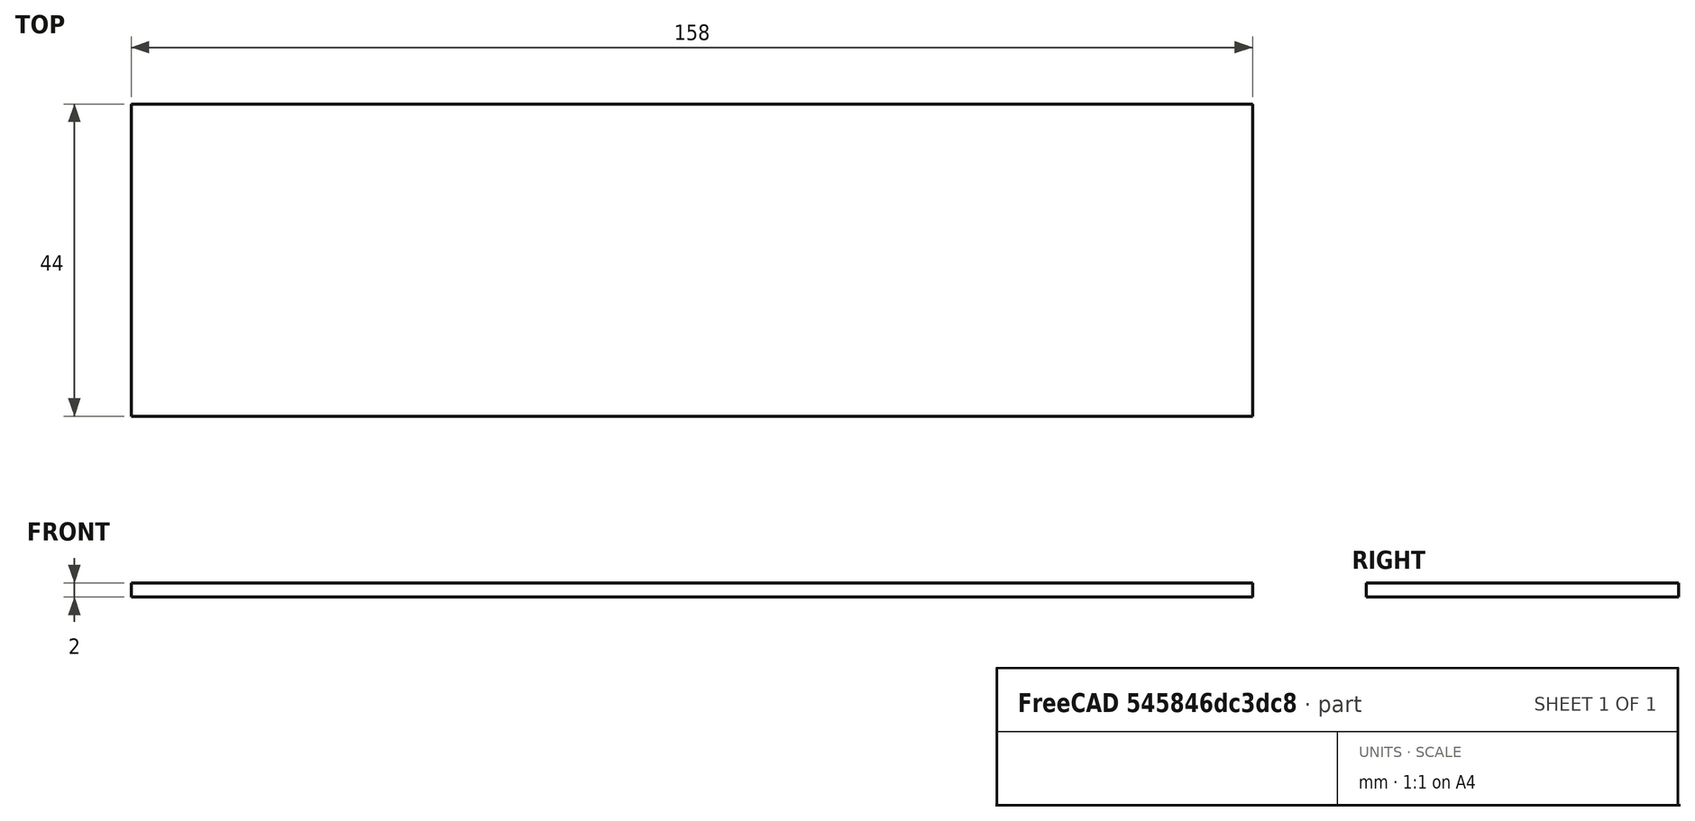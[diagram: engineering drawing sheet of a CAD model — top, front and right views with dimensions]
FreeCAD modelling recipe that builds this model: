
FCSTD DOCUMENT  (FreeCAD 0.21R33771 (Git))
Label: design attempt 1.1
License: All rights reserved
LicenseURL: https://en.wikipedia.org/wiki/All_rights_reserved
objects: Sketcher::SketchObject×2, PartDesign::Pad×1, PartDesign::Body×1
note: 5 computed .brp shape members not serialized (recipe doc carries the construction recipe); baked Part::Feature solids carry a one-line shape summary decoded from their .brp

FEATURE [Sketcher::SketchObject] Sketch
  FullyConstrained = false
  MapMode = 5
  Support = -> [XY_Plane]
  sketch-geometry (116):
    g0: LineSegment StartX=0 StartY=44 StartZ=0 EndX=20 EndY=44 EndZ=0
    g1: LineSegment StartX=158 StartY=0 StartZ=0 EndX=138 EndY=0 EndZ=0
    g2: LineSegment StartX=158 StartY=44 StartZ=0 EndX=138 EndY=44 EndZ=0
    g3: LineSegment StartX=1 StartY=2 StartZ=0 EndX=1 EndY=6.3 EndZ=0
    g4: LineSegment StartX=1 StartY=6.3 StartZ=0 EndX=2 EndY=6.3 EndZ=0
    g5: LineSegment StartX=2 StartY=6.3 StartZ=0 EndX=2 EndY=2 EndZ=0
    g6: LineSegment StartX=20 StartY=21 StartZ=0 EndX=20 EndY=23 EndZ=0
    g7: LineSegment StartX=1 StartY=21 StartZ=0 EndX=1 EndY=16.7 EndZ=0
    g8: LineSegment StartX=1 StartY=16.7 StartZ=0 EndX=2 EndY=16.7 EndZ=0
    g9: LineSegment StartX=2 StartY=16.7 StartZ=0 EndX=2 EndY=21 EndZ=0
    g10: LineSegment StartX=76.5 StartY=2 StartZ=0 EndX=76.5 EndY=6.3 EndZ=0
    g11: LineSegment StartX=76.5 StartY=6.3 StartZ=0 EndX=75.5 EndY=6.3 EndZ=0
    g12: LineSegment StartX=75.5 StartY=6.3 StartZ=0 EndX=75.5 EndY=2 EndZ=0
    g13: LineSegment StartX=77.5 StartY=0 StartZ=0 EndX=79.5 EndY=0 EndZ=0
    g14: LineSegment StartX=79.4989 StartY=44 StartZ=0 EndX=77.4989 EndY=44 EndZ=0
    g15: LineSegment StartX=77.5 StartY=0 StartZ=0 EndX=57.5 EndY=0 EndZ=0
    g16: LineSegment StartX=76.5 StartY=21 StartZ=0 EndX=76.5 EndY=16.7 EndZ=0
    g17: LineSegment StartX=76.5 StartY=16.7 StartZ=0 EndX=75.5 EndY=16.7 EndZ=0
    g18: LineSegment StartX=75.5 StartY=16.7 StartZ=0 EndX=75.5 EndY=21 EndZ=0
    g19: LineSegment StartX=57.5 StartY=21 StartZ=0 EndX=57.5 EndY=23 EndZ=0
    g20: LineSegment StartX=2 StartY=23 StartZ=0 EndX=2 EndY=27.3 EndZ=0
    g21: LineSegment StartX=2 StartY=27.3 StartZ=0 EndX=1 EndY=27.3 EndZ=0
    g22: LineSegment StartX=1 StartY=27.3 StartZ=0 EndX=1 EndY=23 EndZ=0
    g23: LineSegment StartX=2 StartY=42 StartZ=0 EndX=2 EndY=37.7 EndZ=0
    g24: LineSegment StartX=2 StartY=37.7 StartZ=0 EndX=1 EndY=37.7 EndZ=0
    g25: LineSegment StartX=1 StartY=37.7 StartZ=0 EndX=1 EndY=42 EndZ=0
    g26: LineSegment StartX=57.5 StartY=44 StartZ=0 EndX=77.5 EndY=44 EndZ=0
    g27: LineSegment StartX=76.5 StartY=23 StartZ=0 EndX=76.5 EndY=27.3 EndZ=0
    g28: LineSegment StartX=76.5 StartY=27.3 StartZ=0 EndX=75.5 EndY=27.3 EndZ=0
    g29: LineSegment StartX=75.5 StartY=27.3 StartZ=0 EndX=75.5 EndY=23 EndZ=0
    g30: LineSegment StartX=75.5 StartY=42 StartZ=0 EndX=75.5 EndY=37.7 EndZ=0
    g31: LineSegment StartX=75.5 StartY=37.7 StartZ=0 EndX=76.5 EndY=37.7 EndZ=0
    g32: LineSegment StartX=76.5 StartY=37.7 StartZ=0 EndX=76.5 EndY=42 EndZ=0
    g33: LineSegment StartX=79.5 StartY=0 StartZ=0 EndX=99.5 EndY=0 EndZ=0
    g34: LineSegment StartX=79.5 StartY=44 StartZ=0 EndX=99.5 EndY=44 EndZ=0
    g35: LineSegment StartX=99.5 StartY=23 StartZ=0 EndX=99.5 EndY=21 EndZ=0
    g36: LineSegment StartX=138 StartY=21 StartZ=0 EndX=138 EndY=23 EndZ=0
    g37: LineSegment StartX=81.5 StartY=2 StartZ=0 EndX=81.5 EndY=6.3 EndZ=0
    g38: LineSegment StartX=81.5 StartY=6.3 StartZ=0 EndX=80.5 EndY=6.3 EndZ=0
    g39: LineSegment StartX=80.5 StartY=6.3 StartZ=0 EndX=80.5 EndY=2 EndZ=0
    g40: LineSegment StartX=81.5 StartY=21 StartZ=0 EndX=81.5 EndY=16.7 EndZ=0
    g41: LineSegment StartX=81.5 StartY=16.7 StartZ=0 EndX=80.5 EndY=16.7 EndZ=0
    g42: LineSegment StartX=80.5 StartY=16.7 StartZ=0 EndX=80.5 EndY=21 EndZ=0
    g43: LineSegment StartX=80.5 StartY=23 StartZ=0 EndX=80.5 EndY=27.3 EndZ=0
    g44: LineSegment StartX=80.5 StartY=27.3 StartZ=0 EndX=81.5 EndY=27.3 EndZ=0
    g45: LineSegment StartX=81.5 StartY=27.3 StartZ=0 EndX=81.5 EndY=23 EndZ=0
    g46: LineSegment StartX=156 StartY=2 StartZ=0 EndX=156 EndY=6.3 EndZ=0
    g47: LineSegment StartX=156 StartY=6.3 StartZ=0 EndX=157 EndY=6.3 EndZ=0
    g48: LineSegment StartX=157 StartY=6.3 StartZ=0 EndX=157 EndY=2 EndZ=0
    g49: LineSegment StartX=156 StartY=21 StartZ=0 EndX=156 EndY=16.7 EndZ=0
    g50: LineSegment StartX=156 StartY=16.7 StartZ=0 EndX=157 EndY=16.7 EndZ=0
    g51: LineSegment StartX=157 StartY=16.7 StartZ=0 EndX=157 EndY=21 EndZ=0
    g52: LineSegment StartX=156 StartY=23 StartZ=0 EndX=156 EndY=27.3 EndZ=0
    g53: LineSegment StartX=156 StartY=27.3 StartZ=0 EndX=157 EndY=27.3 EndZ=0
    g54: LineSegment StartX=157 StartY=27.3 StartZ=0 EndX=157 EndY=23 EndZ=0
    g55: LineSegment StartX=156 StartY=42 StartZ=0 EndX=156 EndY=37.7 EndZ=0
    g56: LineSegment StartX=156 StartY=37.7 StartZ=0 EndX=157 EndY=37.7 EndZ=0
    g57: LineSegment StartX=157 StartY=37.7 StartZ=0 EndX=157 EndY=42 EndZ=0
    g58: LineSegment StartX=81.5 StartY=42 StartZ=0 EndX=81.5 EndY=37.7 EndZ=0
    g59: LineSegment StartX=81.5 StartY=37.7 StartZ=0 EndX=80.5 EndY=37.7 EndZ=0
    g60: LineSegment StartX=80.5 StartY=37.7 StartZ=0 EndX=80.5 EndY=42 EndZ=0
    g61: LineSegment StartX=0 StartY=2 StartZ=0 EndX=1 EndY=2 EndZ=0
    g62: LineSegment StartX=2 StartY=2 StartZ=0 EndX=20 EndY=2 EndZ=0
    g63: LineSegment StartX=20 StartY=0 StartZ=0 EndX=2e-06 EndY=0 EndZ=0
    g64: LineSegment StartX=0 StartY=23 StartZ=0 EndX=1 EndY=23 EndZ=0
    g65: LineSegment StartX=2 StartY=23 StartZ=0 EndX=20 EndY=23 EndZ=0
    g66: LineSegment StartX=20 StartY=21 StartZ=0 EndX=2 EndY=21 EndZ=0
    g67: LineSegment StartX=1 StartY=21 StartZ=0 EndX=0 EndY=21 EndZ=0
    g68: LineSegment StartX=0 StartY=42 StartZ=0 EndX=1 EndY=42 EndZ=0
    g69: LineSegment StartX=2 StartY=42 StartZ=0 EndX=20 EndY=42 EndZ=0
    g70: LineSegment StartX=77.5 StartY=42 StartZ=0 EndX=76.5 EndY=42 EndZ=0
    g71: LineSegment StartX=75.5 StartY=42 StartZ=0 EndX=57.5 EndY=42 EndZ=0
    g72: LineSegment StartX=79.5 StartY=42 StartZ=0 EndX=80.5 EndY=42 EndZ=0
    g73: LineSegment StartX=81.5 StartY=42 StartZ=0 EndX=99.5 EndY=42 EndZ=0
    g74: LineSegment StartX=77.5001 StartY=42 StartZ=0 EndX=77.5001 EndY=23 EndZ=0
    g75: LineSegment StartX=79.5 StartY=23 StartZ=0 EndX=79.5 EndY=42 EndZ=0
    g76: LineSegment StartX=79.5 StartY=2 StartZ=0 EndX=79.5 EndY=21 EndZ=0
    g77: LineSegment StartX=77.5 StartY=21 StartZ=0 EndX=77.5 EndY=2 EndZ=0
    g78: LineSegment StartX=77.5001 StartY=23 StartZ=0 EndX=76.5001 EndY=23 EndZ=0
    g79: LineSegment StartX=75.5 StartY=23 StartZ=0 EndX=57.5 EndY=23 EndZ=0
    g80: LineSegment StartX=57.5 StartY=21 StartZ=0 EndX=75.5 EndY=21 EndZ=0
    g81: LineSegment StartX=76.5 StartY=21 StartZ=0 EndX=77.5 EndY=21 EndZ=0
    g82: LineSegment StartX=79.5 StartY=21 StartZ=0 EndX=80.5 EndY=21 EndZ=0
    g83: LineSegment StartX=79.5 StartY=23 StartZ=0 EndX=80.5 EndY=23 EndZ=0
    g84: LineSegment StartX=81.5 StartY=23 StartZ=0 EndX=99.5 EndY=23 EndZ=0
    g85: LineSegment StartX=99.5 StartY=21 StartZ=0 EndX=81.5 EndY=21 EndZ=0
    g86: LineSegment StartX=77.5 StartY=2 StartZ=0 EndX=76.5 EndY=2 EndZ=0
    g87: LineSegment StartX=75.5 StartY=2 StartZ=0 EndX=57.5 EndY=2 EndZ=0
    g88: LineSegment StartX=79.5 StartY=2 StartZ=0 EndX=80.5 EndY=2 EndZ=0
    g89: LineSegment StartX=81.5 StartY=2 StartZ=0 EndX=99.5 EndY=2 EndZ=0
    g90: LineSegment StartX=158 StartY=2 StartZ=0 EndX=157 EndY=2 EndZ=0
    g91: LineSegment StartX=156 StartY=2 StartZ=0 EndX=138 EndY=2 EndZ=0
    g92: LineSegment StartX=158 StartY=23 StartZ=0 EndX=157 EndY=23 EndZ=0
    g93: LineSegment StartX=156 StartY=23 StartZ=0 EndX=138 EndY=23 EndZ=0
    g94: LineSegment StartX=138 StartY=21 StartZ=0 EndX=156 EndY=21 EndZ=0
    g95: LineSegment StartX=157 StartY=21 StartZ=0 EndX=158 EndY=21 EndZ=0
    g96: LineSegment StartX=158 StartY=42 StartZ=0 EndX=157 EndY=42 EndZ=0
    g97: LineSegment StartX=156 StartY=42 StartZ=0 EndX=138 EndY=42 EndZ=0
    g98: LineSegment StartX=158 StartY=2 StartZ=0 EndX=158 EndY=21 EndZ=0
    g99: LineSegment StartX=158 StartY=23 StartZ=0 EndX=158 EndY=42 EndZ=0
    g100: LineSegment StartX=0 StartY=42 StartZ=0 EndX=0 EndY=23 EndZ=0
    g101: LineSegment StartX=0 StartY=21 StartZ=0 EndX=0 EndY=2 EndZ=0
    g102: LineSegment StartX=0 StartY=0 StartZ=0 EndX=-8.5 EndY=0 EndZ=0
    g103: LineSegment StartX=-8.5 StartY=0 StartZ=0 EndX=-8.5 EndY=44 EndZ=0
    g104: LineSegment StartX=-8.5 StartY=44 StartZ=0 EndX=0 EndY=44 EndZ=0
    g105: LineSegment StartX=158 StartY=44 StartZ=0 EndX=166.5 EndY=44 EndZ=0
    g106: LineSegment StartX=166.5 StartY=44 StartZ=0 EndX=166.5 EndY=0 EndZ=0
    g107: LineSegment StartX=166.5 StartY=0 StartZ=0 EndX=158 EndY=0 EndZ=0
    g108: LineSegment StartX=138 StartY=0 StartZ=0 EndX=99.5 EndY=0 EndZ=0
    g109: LineSegment StartX=99.5 StartY=2 StartZ=0 EndX=138 EndY=2 EndZ=0
    g110: LineSegment StartX=20 StartY=2 StartZ=0 EndX=57.5 EndY=2 EndZ=0
    g111: LineSegment StartX=57.5 StartY=0 StartZ=0 EndX=20 EndY=0 EndZ=0
    g112: LineSegment StartX=138 StartY=44 StartZ=0 EndX=99.5 EndY=44 EndZ=0
    g113: LineSegment StartX=99.5 StartY=42 StartZ=0 EndX=138 EndY=42 EndZ=0
    g114: LineSegment StartX=20 StartY=44 StartZ=0 EndX=57.5 EndY=44 EndZ=0
    g115: LineSegment StartX=57.5 StartY=42 StartZ=0 EndX=20 EndY=42 EndZ=0
  constraints (313):
    c: Horizontal(g0)
    c: Horizontal(g1)
    c: Horizontal(g2)
    c: Coincident(g3,g4)
    c: Coincident(g4,g5)
    c: Horizontal(g4)
    c: Vertical(g3)
    c: Vertical(g5)
    c: Vertical(g6)
    c: Coincident(g7,g8)
    c: Coincident(g8,g9)
    c: Horizontal(g8)
    c: Vertical(g7)
    c: Vertical(g9)
    c: Coincident(g11,g12)
    c: Horizontal(g11)
    c: Vertical(g10)
    c: Vertical(g12)
    c: Horizontal(g13)
    c: Horizontal(g14)
    c: Horizontal(g15)
    c: Coincident(g15,g13)
    c: Coincident(g16,g17)
    c: Coincident(g17,g18)
    c: Horizontal(g17)
    c: Vertical(g16)
    c: Vertical(g18)
    c: Vertical(g19)
    c: Coincident(g20,g21)
    c: Coincident(g21,g22)
    c: Horizontal(g21)
    c: Vertical(g20)
    c: Vertical(g22)
    c: Coincident(g23,g24)
    c: Coincident(g24,g25)
    c: Horizontal(g24)
    c: Vertical(g23)
    c: Vertical(g25)
    c: Horizontal(g26)
    c: Coincident(g27,g28)
    c: Coincident(g28,g29)
    c: Horizontal(g28)
    c: Vertical(g27)
    c: Vertical(g29)
    c: Coincident(g30,g31)
    c: Coincident(g31,g32)
    c: Horizontal(g31)
    c: Vertical(g30)
    c: Vertical(g32)
    c: Horizontal(g33)
    c: Coincident(g33,g13)
    c: Horizontal(g34)
    c: Vertical(g35)
    c: Vertical(g36)
    c: Coincident(g37,g38)
    c: Coincident(g38,g39)
    c: Horizontal(g38)
    c: Vertical(g37)
    c: Vertical(g39)
    c: Coincident(g40,g41)
    c: Coincident(g41,g42)
    c: Horizontal(g41)
    c: Vertical(g40)
    c: Vertical(g42)
    c: Coincident(g43,g44)
    c: Coincident(g44,g45)
    c: Horizontal(g44)
    c: Vertical(g43)
    c: Vertical(g45)
    c: Coincident(g46,g47)
    c: Coincident(g47,g48)
    c: Horizontal(g47)
    c: Vertical(g46)
    c: Vertical(g48)
    c: Coincident(g49,g50)
    c: Coincident(g50,g51)
    c: Horizontal(g50)
    c: Vertical(g49)
    c: Vertical(g51)
    c: Coincident(g52,g53)
    c: Coincident(g53,g54)
    c: Horizontal(g53)
    c: Vertical(g52)
    c: Vertical(g54)
    c: Coincident(g55,g56)
    c: Coincident(g56,g57)
    c: Horizontal(g56)
    c: Vertical(g55)
    c: Vertical(g57)
    c: Coincident(g58,g59)
    c: Coincident(g59,g60)
    c: Horizontal(g59)
    c: Vertical(g58)
    c: Vertical(g60)
    c: PointOnObject(g61,g-2)
    c: Horizontal(g61)
    c: Coincident(g5,g62)
    c: Horizontal(g62)
    c: Horizontal(g63)
    c: Coincident(g64,g22)
    c: Horizontal(g64)
    c: Coincident(g65,g6)
    c: Horizontal(g65)
    c: Coincident(g6,g66)
    c: Coincident(g66,g9)
    c: Horizontal(g66)
    c: Coincident(g7,g67)
    c: Horizontal(g67)
    c: Horizontal(g68)
    c: Horizontal(g69)
    c: Horizontal(g70)
    c: DistanceX(g31,g31) = 1
    c: Coincident(g30,g71)
    c: Horizontal(g71)
    c: Coincident(g72,g60)
    c: Horizontal(g72)
    c: Coincident(g58,g73)
    c: Horizontal(g73)
    c: Vertical(g74)
    c: Vertical(g75)
    c: Vertical(g76)
    c: Vertical(g77)
    c: Coincident(g74,g78)
    c: Horizontal(g78)
    c: Coincident(g29,g79)
    c: Coincident(g79,g19)
    c: Horizontal(g79)
    c: Coincident(g19,g80)
    c: Horizontal(g80)
    c: Coincident(g16,g81)
    c: Coincident(g81,g77)
    c: Horizontal(g81)
    c: Coincident(g76,g82)
    c: Coincident(g82,g42)
    c: Horizontal(g82)
    c: Coincident(g75,g83)
    c: Coincident(g83,g43)
    c: Horizontal(g83)
    c: Coincident(g45,g84)
    c: Coincident(g84,g35)
    c: Horizontal(g84)
    c: Coincident(g35,g85)
    c: Coincident(g85,g40)
    c: Horizontal(g85)
    c: Coincident(g77,g86)
    c: Coincident(g86,g10)
    c: Horizontal(g86)
    c: Coincident(g12,g87)
    c: Horizontal(g87)
    c: Coincident(g76,g88)
    c: Coincident(g88,g39)
    c: Horizontal(g88)
    c: Coincident(g37,g89)
    c: Horizontal(g89)
    c: Coincident(g90,g48)
    c: Horizontal(g90)
    c: Coincident(g46,g91)
    c: Horizontal(g91)
    c: Coincident(g92,g54)
    c: Horizontal(g92)
    c: Coincident(g52,g93)
    c: Coincident(g93,g36)
    c: Horizontal(g93)
    c: Coincident(g36,g94)
    c: Coincident(g94,g49)
    c: Horizontal(g94)
    c: Coincident(g51,g95)
    c: Horizontal(g95)
    c: Coincident(g96,g57)
    c: Horizontal(g96)
    c: Coincident(g55,g97)
    c: Horizontal(g97)
    c: DistanceX(g59,g59) = 1
    c: DistanceX(g73,g73) = 18
    c: DistanceX(g72,g72) = 1
    c: DistanceX(g70,g70) = 1
    c: DistanceX(g71,g71) = 18
    c: DistanceX(g26,g26) = 20
    c: DistanceX(g28,g28) = 1
    c: DistanceX(g78,g78) = 1
    c: DistanceX(g79,g79) = 18
    c: DistanceX(g80,g80) = 18
    c: DistanceX(g17,g17) = 1
    c: DistanceX(g81,g81) = 1
    c: DistanceX(g83,g83) = 1
    c: DistanceX(g44,g44) = 1
    c: DistanceX(g84,g84) = 18
    c: DistanceX(g85,g85) = 18
    c: DistanceX(g41,g41) = 1
    c: DistanceX(g82,g82) = 1
    c: DistanceX(g86,g86) = 1
    c: DistanceX(g11,g11) = 1
    c: DistanceX(g87,g87) = 18
    c: DistanceX(g15,g15) = 20
    c: DistanceX(g33,g33) = 20
    c: DistanceX(g89,g89) = 18
    c: DistanceX(g38,g38) = 1
    c: DistanceX(g88,g88) = 1
    c: DistanceY(g76,g76) = 19
    c: DistanceY(g37,g37) = 4.3
    c: DistanceY(g39,g39) = 4.3
    c: DistanceY(g10,g10) = 4.3
    c: DistanceY(g12,g12) = 4.3
    c: DistanceY(g77,g77) = 19
    c: DistanceY(g42,g42) = 4.3
    c: DistanceY(g16,g16) = 4.3
    c: DistanceY(g40,g40) = 4.3
    c: DistanceY(g18,g18) = 4.3
    c: DistanceY(g27,g27) = 4.3
    c: DistanceY(g29,g29) = 4.3
    c: DistanceY(g43,g43) = 4.3
    c: DistanceY(g45,g45) = 4.3
    c: DistanceY(g75,g75) = 19
    c: DistanceY(g74,g74) = 19
    c: DistanceY(g19,g19) = 2
    c: DistanceY(g35,g35) = 2
    c: DistanceY(g60,g60) = 4.3
    c: DistanceY(g58,g58) = 4.3
    c: DistanceY(g32,g32) = 4.3
    c: DistanceY(g30,g30) = 4.3
    c: DistanceX(g14,g14) = 2
    c: DistanceX(g56,g56) = 1
    c: DistanceX(g96,g96) = 1
    c: DistanceX(g2,g2) = 20
    c: DistanceY(g57,g57) = 4.3
    c: DistanceY(g55,g55) = 4.3
    c: DistanceY(g54,g54) = 4.3
    c: DistanceY(g52,g52) = 4.3
    c: DistanceY(g95,g92) = 2
    c: DistanceY(g36,g36) = 2
    c: DistanceY(g49,g49) = 4.3
    c: DistanceX(g94,g94) = 18
    c: DistanceX(g95,g95) = 1
    c: DistanceX(g92,g92) = 1
    c: DistanceX(g93,g93) = 18
    c: DistanceX(g53,g53) = 1
    c: DistanceY(g46,g46) = 4.3
    c: DistanceY(g48,g48) = 4.3
    c: DistanceX(g91,g91) = 18
    c: DistanceX(g1,g1) = 20
    c: DistanceX(g90,g90) = 1
    c: DistanceX(g62,g62) = 18
    c: DistanceX(g63,g63) = 20
    c: DistanceX(g61,g61) = 1
    c: DistanceX(g4,g4) = 1
    c: DistanceY(g-1,g61) = 2
    c: DistanceY(g5,g5) = 4.3
    c: DistanceY(g3,g3) = 4.3
    c: DistanceY(g6,g6) = 2
    c: DistanceY(g67,g64) = 2
    c: DistanceY(g9,g9) = 4.3
    c: DistanceY(g20,g20) = 4.3
    c: DistanceX(g8,g8) = 1
    c: DistanceX(g67,g67) = 1
    c: DistanceX(g64,g64) = 1
    c: DistanceX(g21,g21) = 1
    c: DistanceX(g65,g65) = 18
    c: DistanceX(g24,g24) = 1
    c: DistanceX(g0,g0) = 20
    c: DistanceX(g68,g68) = 1
    c: DistanceX(g69,g69) = 18
    c: DistanceY(g23,g23) = 4.3
    c: DistanceY(g25,g25) = 4.3
    c: DistanceY(g68,g0) = 2
    c: Vertical(g98)
    c: Vertical(g99)
    c: Vertical(g100)
    c: Vertical(g101)
    c: DistanceX(g0,g26) = 37.5
    c: DistanceY(g100,g100) = 19
    c: DistanceY(g101,g101) = 19
    c: DistanceY(g99,g99) = 19
    c: DistanceY(g98,g98) = 19
    c: PointOnObject(g102,g-1)
    c: Coincident(g102,g103)
    c: Vertical(g103)
    c: Coincident(g103,g104)
    c: Coincident(g104,g0)
    c: Horizontal(g104)
    c: DistanceX(g104,g104) = 8.5
    c: DistanceX(g102,g102) = 8.5
    c: Coincident(g2,g105)
    c: Horizontal(g105)
    c: Coincident(g105,g106)
    c: PointOnObject(g106,g-1)
    c: Vertical(g106)
    c: Coincident(g106,g107)
    c: Coincident(g107,g1)
    c: Horizontal(g107)
    c: DistanceX(g107,g107) = 8.5
    c: Coincident(g1,g108)
    c: Coincident(g108,g33)
    c: Horizontal(g108)
    c: Coincident(g109,g91)
    c: Horizontal(g109)
    c: DistanceX(g109,g109) = 38.5
    c: DistanceX(g108,g108) = 38.5
    c: Coincident(g62,g110)
    c: Horizontal(g110)
    c: Coincident(g15,g111)
    c: Horizontal(g111)
    c: Coincident(g2,g112)
    c: Coincident(g112,g34)
    c: Horizontal(g112)
    c: Coincident(g73,g113)
    c: Coincident(g113,g97)
    c: Horizontal(g113)
    c: Coincident(g0,g114)
    c: Coincident(g114,g26)
    c: Horizontal(g114)
    c: Coincident(g71,g115)
    c: Coincident(g115,g69)
    c: Horizontal(g115)
FEATURE [Sketcher::SketchObject] Sketch004
  FullyConstrained = true
  MapMode = 5
  Support = -> [XY_Plane]
  sketch-geometry (4):
    g0: LineSegment StartX=0 StartY=0 StartZ=0 EndX=158 EndY=0 EndZ=0
    g1: LineSegment StartX=158 StartY=0 StartZ=0 EndX=158 EndY=44 EndZ=0
    g2: LineSegment StartX=158 StartY=44 StartZ=0 EndX=0 EndY=44 EndZ=0
    g3: LineSegment StartX=0 StartY=44 StartZ=0 EndX=0 EndY=0 EndZ=0
  constraints (11):
    c: Coincident(g0,g1)
    c: Coincident(g1,g2)
    c: Coincident(g2,g3)
    c: Coincident(g3,g0)
    c: Horizontal(g0)
    c: Horizontal(g2)
    c: Vertical(g1)
    c: Vertical(g3)
    c: Coincident(g0,g-1)
    c: DistanceY(g1,g1) = 44
    c: DistanceX(g2,g2) = 158
FEATURE [PartDesign::Pad] Pad
  Direction = (0,0,1)
  Length = 2
  Length2 = 10
  Profile = -> Sketch004
  ReferenceAxis = -> Sketch004 [N_Axis]
  Reversed = true
  Type = 0
FEATURE [PartDesign::Body] Body
  Group = -> [Sketch,Sketch004,Pad]
  Origin = -> Origin
  Tip = -> Pad
